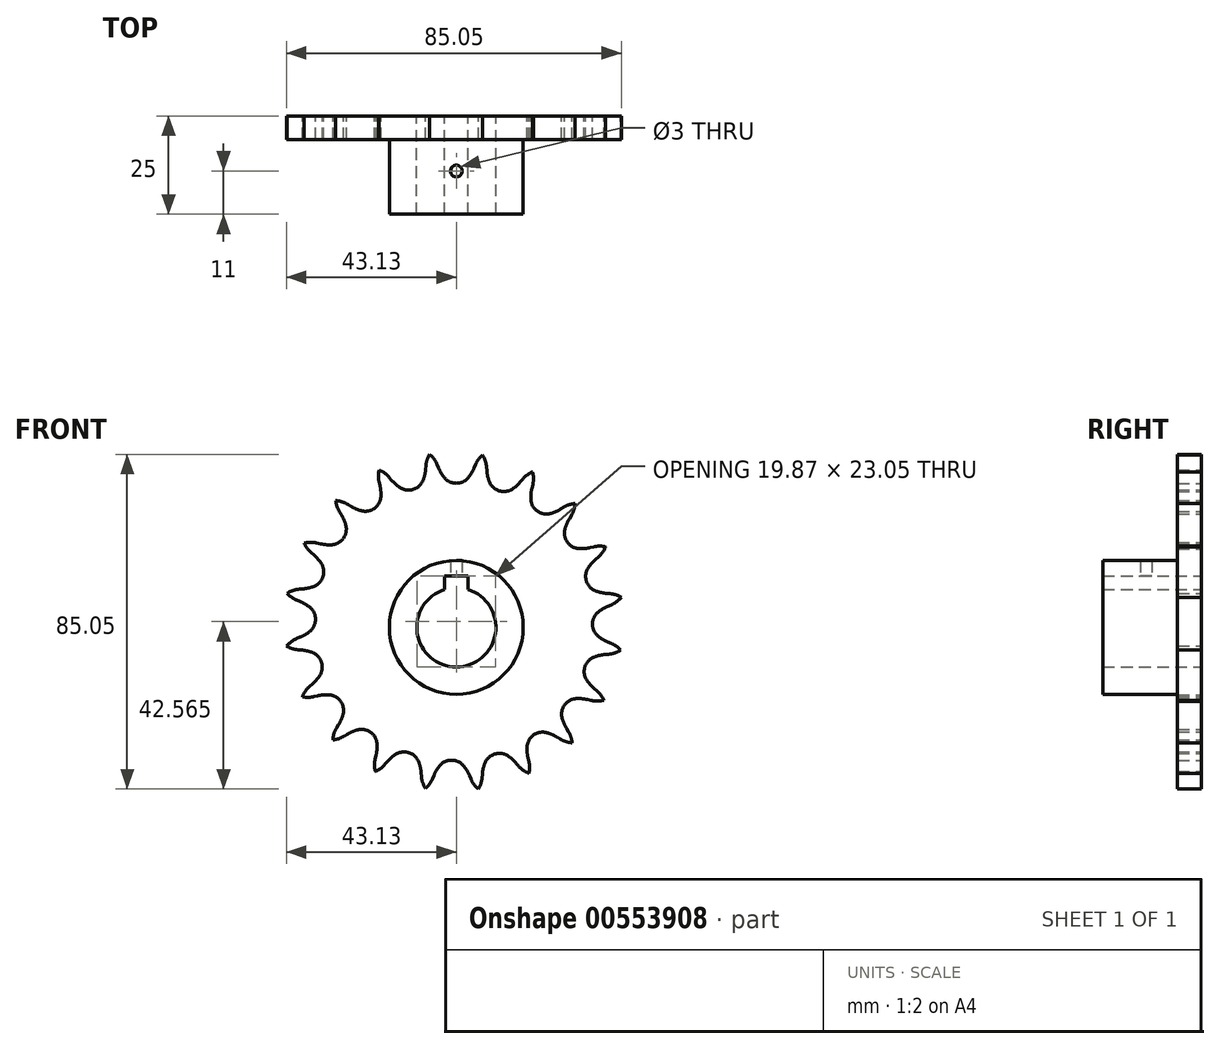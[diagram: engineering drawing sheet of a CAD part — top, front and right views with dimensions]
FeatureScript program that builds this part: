
annotation { "Feature Type Name" : "Feature", "Feature Type Description" : "" }
export const myFeature = defineFeature(function(context is Context, id is Id, definition is map)
    precondition{}
    {
        {
            var Q0;
            Q0=qCreatedBy(makeId("Front.planeOp"),FACE);
            var sketch = newSketch(context, id + "F0", { "sketchPlane" : qUnion([Q0])});
            skCircle(sketch, "E0", {"center": v(0, 0) * mm, "radius": 17 * mm});
            skCircle(sketch, "E1", {"center": v(0, 0) * mm, "radius": 10.05 * mm});
            skSolve(sketch);
        }
        {
            var Q0;
            Q0 = qSketchRegion(id + "F0", true);
            extrude(context, id + "F1", {"entities" : qUnion([Q0]), "depth" : 25 * mm, "offsetDistance" : 25 * mm});
        }
        {
            var Q0;
            Q0=qCreatedBy(makeId("Front.planeOp"),FACE);
            var sketch = newSketch(context, id + "F2", { "sketchPlane" : qUnion([Q0])});
            skCircle(sketch, "E2", {"center": v(0, 0) * mm, "radius": 40.6 * mm, "construction": true});
            skLineSegment(sketch, "E3", {"start": v(0, 0) * mm, "end": v(0, 40.6) * mm, "construction": true});
            skLineSegment(sketch, "E4", {"start": v(0, 40.6) * mm, "end": v(46.47, 40.6) * mm, "construction": true});
            skLineSegment(sketch, "E5", {"start": v(0, 40.6) * mm, "end": v(6.22, 44.3) * mm, "construction": true});
            skLineSegment(sketch, "E6", {"start": v(6.22, 44.3) * mm, "end": v(-5.45, 41.58) * mm, "construction": true});
            skLineSegment(sketch, "E7", {"start": v(-5.45, 41.58) * mm, "end": v(-7.28, 49.4) * mm, "construction": true});
            skSolve(sketch);
        }
        {
            var Q0;
            Q0=qCreatedBy(makeId("Front.planeOp"),FACE);
            var sketch = newSketch(context, id + "F3", { "sketchPlane" : qUnion([Q0])});
            skCircle(sketch, "E8", {"center": v(0, 0) * mm, "radius": 40.6 * mm, "construction": true});
            skLineSegment(sketch, "E9", {"start": v(0, 0) * mm, "end": v(0, 40.6) * mm, "construction": true});
            skLineSegment(sketch, "E10", {"start": v(0, 40.6) * mm, "end": v(62.23, 40.6) * mm, "construction": true});
            skArc(sketch, "E11", {"start": v(-3.14, 38.14) * mm, "mid": v(-1.75, 37.01) * mm, "end": v(0, 36.61) * mm});
            skLineSegment(sketch, "E12", {"start": v(0, 40.6) * mm, "end": v(5, 44.5) * mm, "construction": true});
            skLineSegment(sketch, "E13", {"start": v(5, 44.5) * mm, "end": v(-4.52, 40.5) * mm, "construction": true});
            skLineSegment(sketch, "E14", {"start": v(-4.52, 40.5) * mm, "end": v(-4.9, 41.4) * mm});
            skArc(sketch, "E15", {"start": v(-4.52, 40.5) * mm, "mid": v(-3.9, 39.27) * mm, "end": v(-3.14, 38.14) * mm});
            skArc(sketch, "E16", {"start": v(-4.9, 41.4) * mm, "mid": v(-5.76, 42.88) * mm, "end": v(-6.98, 44.09) * mm});
            skLineSegment(sketch, "E17", {"start": v(0, 0) * mm, "end": v(-9.35, 59.04) * mm, "construction": true});
            skLineSegment(sketch, "E18.trimOffspring", {"start": v(-7.56, 47.73) * mm, "end": v(-8.23, 49.33) * mm, "construction": true});
            skArc(sketch, "E19.trimOffspring", {"start": v(-3.98, 40.72) * mm, "mid": v(-3.98, 40.56) * mm, "end": v(-3.98, 40.4) * mm});
            skArc(sketch, "E20.trimOffspring", {"start": v(3.98, 40.4) * mm, "mid": v(3.98, 40.5) * mm, "end": v(3.98, 40.6) * mm});
            skArc(sketch, "E21.MirrorCS", {"start": v(3.14, 38.14) * mm, "mid": v(1.75, 37.01) * mm, "end": v(0, 36.61) * mm});
            skArc(sketch, "E22.MirrorCS", {"start": v(4.52, 40.5) * mm, "mid": v(3.9, 39.27) * mm, "end": v(3.14, 38.14) * mm});
            skLineSegment(sketch, "E23.MirrorCS", {"start": v(4.52, 40.5) * mm, "end": v(4.9, 41.4) * mm});
            skArc(sketch, "E24.MirrorCS", {"start": v(4.9, 41.4) * mm, "mid": v(5.76, 42.88) * mm, "end": v(6.98, 44.09) * mm});
            skArc(sketch, "E25.1.0", {"start": v(-17.04, 38.12) * mm, "mid": v(-18.32, 39.26) * mm, "end": v(-19.85, 40.03) * mm});
            skArc(sketch, "E25.1.1", {"start": v(-16.4, 37.37) * mm, "mid": v(-15.44, 36.4) * mm, "end": v(-14.36, 35.56) * mm});
            skArc(sketch, "E25.1.2", {"start": v(-14.36, 35.56) * mm, "mid": v(-12.68, 34.92) * mm, "end": v(-10.9, 35.08) * mm});
            skLineSegment(sketch, "E25.1.3", {"start": v(-16.4, 37.37) * mm, "end": v(-17.04, 38.12) * mm});
            skArc(sketch, "E25.1.4", {"start": v(-8.39, 37.5) * mm, "mid": v(-9.37, 36) * mm, "end": v(-10.9, 35.08) * mm});
            skArc(sketch, "E25.1.5", {"start": v(-7.8, 40.17) * mm, "mid": v(-8, 38.81) * mm, "end": v(-8.39, 37.5) * mm});
            skLineSegment(sketch, "E25.1.6", {"start": v(-7.8, 40.17) * mm, "end": v(-7.72, 41.14) * mm});
            skArc(sketch, "E25.1.7", {"start": v(-7.72, 41.14) * mm, "mid": v(-7.36, 42.82) * mm, "end": v(-6.57, 44.34) * mm});
            skArc(sketch, "E25.2.0", {"start": v(-27.57, 31.24) * mm, "mid": v(-29.14, 31.93) * mm, "end": v(-30.84, 32.19) * mm});
            skArc(sketch, "E25.2.1", {"start": v(-26.73, 30.73) * mm, "mid": v(-25.52, 30.1) * mm, "end": v(-24.23, 29.64) * mm});
            skArc(sketch, "E25.2.2", {"start": v(-24.23, 29.64) * mm, "mid": v(-22.44, 29.55) * mm, "end": v(-20.8, 30.25) * mm});
            skLineSegment(sketch, "E25.2.3", {"start": v(-26.73, 30.73) * mm, "end": v(-27.57, 31.24) * mm});
            skArc(sketch, "E25.2.4", {"start": v(-19.15, 33.33) * mm, "mid": v(-19.62, 31.6) * mm, "end": v(-20.8, 30.25) * mm});
            skArc(sketch, "E25.2.5", {"start": v(-19.42, 36.04) * mm, "mid": v(-19.2, 34.7) * mm, "end": v(-19.15, 33.33) * mm});
            skLineSegment(sketch, "E25.2.6", {"start": v(-19.42, 36.04) * mm, "end": v(-19.64, 37) * mm});
            skArc(sketch, "E25.2.7", {"start": v(-19.64, 37) * mm, "mid": v(-19.81, 38.7) * mm, "end": v(-19.54, 40.4) * mm});
            skArc(sketch, "E25.3.0", {"start": v(-35.46, 21.45) * mm, "mid": v(-37.17, 21.62) * mm, "end": v(-38.86, 21.34) * mm});
            skArc(sketch, "E25.3.1", {"start": v(-34.5, 21.22) * mm, "mid": v(-33.16, 21) * mm, "end": v(-31.8, 20.96) * mm});
            skArc(sketch, "E25.3.2", {"start": v(-31.8, 20.96) * mm, "mid": v(-30.06, 21.42) * mm, "end": v(-28.7, 22.6) * mm});
            skLineSegment(sketch, "E25.3.3", {"start": v(-34.5, 21.22) * mm, "end": v(-35.46, 21.45) * mm});
            skArc(sketch, "E25.3.4", {"start": v(-28.1, 26.03) * mm, "mid": v(-28, 24.25) * mm, "end": v(-28.7, 22.6) * mm});
            skArc(sketch, "E25.3.5", {"start": v(-29.2, 28.53) * mm, "mid": v(-28.57, 27.32) * mm, "end": v(-28.1, 26.03) * mm});
            skLineSegment(sketch, "E25.3.6", {"start": v(-29.2, 28.53) * mm, "end": v(-29.7, 29.38) * mm});
            skArc(sketch, "E25.3.7", {"start": v(-29.7, 29.38) * mm, "mid": v(-30.4, 30.95) * mm, "end": v(-30.65, 32.64) * mm});
            skArc(sketch, "E25.4.0", {"start": v(-39.94, 9.7) * mm, "mid": v(-41.62, 9.33) * mm, "end": v(-43.14, 8.54) * mm});
            skArc(sketch, "E25.4.1", {"start": v(-38.96, 9.78) * mm, "mid": v(-37.61, 9.98) * mm, "end": v(-36.3, 10.36) * mm});
            skArc(sketch, "E25.4.2", {"start": v(-36.3, 10.36) * mm, "mid": v(-34.8, 11.34) * mm, "end": v(-33.87, 12.88) * mm});
            skLineSegment(sketch, "E25.4.3", {"start": v(-38.96, 9.78) * mm, "end": v(-39.94, 9.7) * mm});
            skArc(sketch, "E25.4.4", {"start": v(-34.36, 16.33) * mm, "mid": v(-33.72, 14.66) * mm, "end": v(-33.87, 12.88) * mm});
            skArc(sketch, "E25.4.5", {"start": v(-36.17, 18.37) * mm, "mid": v(-35.2, 17.41) * mm, "end": v(-34.36, 16.33) * mm});
            skLineSegment(sketch, "E25.4.6", {"start": v(-36.17, 18.37) * mm, "end": v(-36.92, 19.01) * mm});
            skArc(sketch, "E25.4.7", {"start": v(-36.92, 19.01) * mm, "mid": v(-38.06, 20.3) * mm, "end": v(-38.83, 21.83) * mm});
            skArc(sketch, "E25.5.0", {"start": v(-40.57, -2.87) * mm, "mid": v(-42.05, -3.73) * mm, "end": v(-43.26, -4.95) * mm});
            skArc(sketch, "E25.5.1", {"start": v(-39.66, -2.48) * mm, "mid": v(-38.44, -1.87) * mm, "end": v(-37.31, -1.1) * mm});
            skArc(sketch, "E25.5.2", {"start": v(-37.31, -1.1) * mm, "mid": v(-36.18, 0.29) * mm, "end": v(-35.78, 2.03) * mm});
            skLineSegment(sketch, "E25.5.3", {"start": v(-39.66, -2.48) * mm, "end": v(-40.57, -2.87) * mm});
            skArc(sketch, "E25.5.4", {"start": v(-37.31, 5.17) * mm, "mid": v(-36.18, 3.78) * mm, "end": v(-35.78, 2.03) * mm});
            skArc(sketch, "E25.5.5", {"start": v(-39.66, 6.55) * mm, "mid": v(-38.44, 5.94) * mm, "end": v(-37.31, 5.17) * mm});
            skLineSegment(sketch, "E25.5.6", {"start": v(-39.66, 6.55) * mm, "end": v(-40.57, 6.93) * mm});
            skArc(sketch, "E25.5.7", {"start": v(-40.57, 6.93) * mm, "mid": v(-42.05, 7.8) * mm, "end": v(-43.26, 9.02) * mm});
            skArc(sketch, "E25.6.0", {"start": v(-37.29, -15) * mm, "mid": v(-38.43, -16.29) * mm, "end": v(-39.2, -17.82) * mm});
            skArc(sketch, "E25.6.1", {"start": v(-36.54, -14.36) * mm, "mid": v(-35.57, -13.4) * mm, "end": v(-34.73, -12.32) * mm});
            skArc(sketch, "E25.6.2", {"start": v(-34.73, -12.32) * mm, "mid": v(-34.09, -10.65) * mm, "end": v(-34.25, -8.87) * mm});
            skLineSegment(sketch, "E25.6.3", {"start": v(-36.54, -14.36) * mm, "end": v(-37.29, -15) * mm});
            skArc(sketch, "E25.6.4", {"start": v(-36.67, -6.36) * mm, "mid": v(-35.17, -7.33) * mm, "end": v(-34.25, -8.87) * mm});
            skArc(sketch, "E25.6.5", {"start": v(-39.34, -5.77) * mm, "mid": v(-37.98, -5.97) * mm, "end": v(-36.67, -6.36) * mm});
            skLineSegment(sketch, "E25.6.6", {"start": v(-39.34, -5.77) * mm, "end": v(-40.31, -5.69) * mm});
            skArc(sketch, "E25.6.7", {"start": v(-40.31, -5.69) * mm, "mid": v(-41.99, -5.32) * mm, "end": v(-43.51, -4.54) * mm});
            skArc(sketch, "E25.7.0", {"start": v(-30.41, -25.54) * mm, "mid": v(-31.1, -27.1) * mm, "end": v(-31.36, -28.8) * mm});
            skArc(sketch, "E25.7.1", {"start": v(-29.9, -24.7) * mm, "mid": v(-29.27, -23.48) * mm, "end": v(-28.8, -22.2) * mm});
            skArc(sketch, "E25.7.2", {"start": v(-28.8, -22.2) * mm, "mid": v(-28.72, -20.4) * mm, "end": v(-29.42, -18.76) * mm});
            skLineSegment(sketch, "E25.7.3", {"start": v(-29.9, -24.7) * mm, "end": v(-30.41, -25.54) * mm});
            skArc(sketch, "E25.7.4", {"start": v(-32.5, -17.12) * mm, "mid": v(-30.77, -17.58) * mm, "end": v(-29.42, -18.76) * mm});
            skArc(sketch, "E25.7.5", {"start": v(-35.21, -17.39) * mm, "mid": v(-33.86, -17.16) * mm, "end": v(-32.5, -17.12) * mm});
            skLineSegment(sketch, "E25.7.6", {"start": v(-35.21, -17.39) * mm, "end": v(-36.17, -17.61) * mm});
            skArc(sketch, "E25.7.7", {"start": v(-36.17, -17.61) * mm, "mid": v(-37.88, -17.78) * mm, "end": v(-39.57, -17.5) * mm});
            skArc(sketch, "E25.8.0", {"start": v(-20.62, -33.43) * mm, "mid": v(-20.79, -35.14) * mm, "end": v(-20.51, -36.83) * mm});
            skArc(sketch, "E25.8.1", {"start": v(-20.4, -32.47) * mm, "mid": v(-20.17, -31.12) * mm, "end": v(-20.13, -29.76) * mm});
            skArc(sketch, "E25.8.2", {"start": v(-20.13, -29.76) * mm, "mid": v(-20.6, -28.03) * mm, "end": v(-21.77, -26.67) * mm});
            skLineSegment(sketch, "E25.8.3", {"start": v(-20.4, -32.47) * mm, "end": v(-20.62, -33.43) * mm});
            skArc(sketch, "E25.8.4", {"start": v(-25.2, -26.07) * mm, "mid": v(-23.42, -25.98) * mm, "end": v(-21.77, -26.67) * mm});
            skArc(sketch, "E25.8.5", {"start": v(-27.7, -27.16) * mm, "mid": v(-26.5, -26.53) * mm, "end": v(-25.2, -26.07) * mm});
            skLineSegment(sketch, "E25.8.6", {"start": v(-27.7, -27.16) * mm, "end": v(-28.55, -27.67) * mm});
            skArc(sketch, "E25.8.7", {"start": v(-28.55, -27.67) * mm, "mid": v(-30.12, -28.36) * mm, "end": v(-31.8, -28.62) * mm});
            skArc(sketch, "E25.9.0", {"start": v(-8.87, -37.9) * mm, "mid": v(-8.5, -39.58) * mm, "end": v(-7.71, -41.1) * mm});
            skArc(sketch, "E25.9.1", {"start": v(-8.95, -36.93) * mm, "mid": v(-9.15, -35.58) * mm, "end": v(-9.53, -34.26) * mm});
            skArc(sketch, "E25.9.2", {"start": v(-9.53, -34.26) * mm, "mid": v(-10.5, -32.76) * mm, "end": v(-12.05, -31.84) * mm});
            skLineSegment(sketch, "E25.9.3", {"start": v(-8.95, -36.93) * mm, "end": v(-8.87, -37.9) * mm});
            skArc(sketch, "E25.9.4", {"start": v(-15.5, -32.33) * mm, "mid": v(-13.83, -31.68) * mm, "end": v(-12.05, -31.84) * mm});
            skArc(sketch, "E25.9.5", {"start": v(-17.54, -34.14) * mm, "mid": v(-16.58, -33.16) * mm, "end": v(-15.5, -32.33) * mm});
            skLineSegment(sketch, "E25.9.6", {"start": v(-17.54, -34.14) * mm, "end": v(-18.18, -34.88) * mm});
            skArc(sketch, "E25.9.7", {"start": v(-18.18, -34.88) * mm, "mid": v(-19.46, -36.02) * mm, "end": v(-21, -36.8) * mm});
            skArc(sketch, "E25.10.0", {"start": v(3.7, -38.54) * mm, "mid": v(4.56, -40.02) * mm, "end": v(5.78, -41.22) * mm});
            skArc(sketch, "E25.10.1", {"start": v(3.31, -37.63) * mm, "mid": v(2.7, -36.4) * mm, "end": v(1.93, -35.28) * mm});
            skArc(sketch, "E25.10.2", {"start": v(1.93, -35.28) * mm, "mid": v(0.54, -34.15) * mm, "end": v(-1.2, -33.75) * mm});
            skLineSegment(sketch, "E25.10.3", {"start": v(3.31, -37.63) * mm, "end": v(3.7, -38.54) * mm});
            skArc(sketch, "E25.10.4", {"start": v(-4.34, -35.28) * mm, "mid": v(-2.95, -34.15) * mm, "end": v(-1.2, -33.75) * mm});
            skArc(sketch, "E25.10.5", {"start": v(-5.72, -37.63) * mm, "mid": v(-5.1, -36.4) * mm, "end": v(-4.34, -35.28) * mm});
            skLineSegment(sketch, "E25.10.6", {"start": v(-5.72, -37.63) * mm, "end": v(-6.1, -38.54) * mm});
            skArc(sketch, "E25.10.7", {"start": v(-6.1, -38.54) * mm, "mid": v(-6.97, -40.02) * mm, "end": v(-8.19, -41.22) * mm});
            skArc(sketch, "E25.11.0", {"start": v(15.84, -35.25) * mm, "mid": v(17.12, -36.4) * mm, "end": v(18.65, -37.16) * mm});
            skArc(sketch, "E25.11.1", {"start": v(15.2, -34.5) * mm, "mid": v(14.23, -33.54) * mm, "end": v(13.15, -32.7) * mm});
            skArc(sketch, "E25.11.2", {"start": v(13.15, -32.7) * mm, "mid": v(11.48, -32.06) * mm, "end": v(9.7, -32.21) * mm});
            skLineSegment(sketch, "E25.11.3", {"start": v(15.2, -34.5) * mm, "end": v(15.84, -35.25) * mm});
            skArc(sketch, "E25.11.4", {"start": v(7.19, -34.64) * mm, "mid": v(8.16, -33.13) * mm, "end": v(9.7, -32.21) * mm});
            skArc(sketch, "E25.11.5", {"start": v(6.6, -37.3) * mm, "mid": v(6.8, -35.95) * mm, "end": v(7.19, -34.64) * mm});
            skLineSegment(sketch, "E25.11.6", {"start": v(6.6, -37.3) * mm, "end": v(6.52, -38.28) * mm});
            skArc(sketch, "E25.11.7", {"start": v(6.52, -38.28) * mm, "mid": v(6.15, -39.96) * mm, "end": v(5.37, -41.48) * mm});
            skArc(sketch, "E25.12.0", {"start": v(26.37, -28.38) * mm, "mid": v(27.94, -29.07) * mm, "end": v(29.63, -29.33) * mm});
            skArc(sketch, "E25.12.1", {"start": v(25.53, -27.87) * mm, "mid": v(24.31, -27.24) * mm, "end": v(23.03, -26.78) * mm});
            skArc(sketch, "E25.12.2", {"start": v(23.03, -26.78) * mm, "mid": v(21.24, -26.68) * mm, "end": v(19.59, -27.38) * mm});
            skLineSegment(sketch, "E25.12.3", {"start": v(25.53, -27.87) * mm, "end": v(26.37, -28.38) * mm});
            skArc(sketch, "E25.12.4", {"start": v(17.95, -30.46) * mm, "mid": v(18.41, -28.73) * mm, "end": v(19.59, -27.38) * mm});
            skArc(sketch, "E25.12.5", {"start": v(18.22, -33.18) * mm, "mid": v(18, -31.83) * mm, "end": v(17.95, -30.46) * mm});
            skLineSegment(sketch, "E25.12.6", {"start": v(18.22, -33.18) * mm, "end": v(18.44, -34.14) * mm});
            skArc(sketch, "E25.12.7", {"start": v(18.44, -34.14) * mm, "mid": v(18.61, -35.84) * mm, "end": v(18.33, -37.53) * mm});
            skArc(sketch, "E25.13.0", {"start": v(34.26, -18.58) * mm, "mid": v(35.97, -18.76) * mm, "end": v(37.66, -18.48) * mm});
            skArc(sketch, "E25.13.1", {"start": v(33.3, -18.36) * mm, "mid": v(31.95, -18.14) * mm, "end": v(30.59, -18.1) * mm});
            skArc(sketch, "E25.13.2", {"start": v(30.59, -18.1) * mm, "mid": v(28.86, -18.56) * mm, "end": v(27.5, -19.73) * mm});
            skLineSegment(sketch, "E25.13.3", {"start": v(33.3, -18.36) * mm, "end": v(34.26, -18.58) * mm});
            skArc(sketch, "E25.13.4", {"start": v(26.9, -23.17) * mm, "mid": v(26.8, -21.38) * mm, "end": v(27.5, -19.73) * mm});
            skArc(sketch, "E25.13.5", {"start": v(28, -25.67) * mm, "mid": v(27.36, -24.46) * mm, "end": v(26.9, -23.17) * mm});
            skLineSegment(sketch, "E25.13.6", {"start": v(28, -25.67) * mm, "end": v(28.5, -26.51) * mm});
            skArc(sketch, "E25.13.7", {"start": v(28.5, -26.51) * mm, "mid": v(29.19, -28.08) * mm, "end": v(29.45, -29.78) * mm});
            skArc(sketch, "E25.14.0", {"start": v(38.74, -6.83) * mm, "mid": v(40.41, -6.47) * mm, "end": v(41.94, -5.68) * mm});
            skArc(sketch, "E25.14.1", {"start": v(37.76, -6.91) * mm, "mid": v(36.4, -7.12) * mm, "end": v(35.1, -7.5) * mm});
            skArc(sketch, "E25.14.2", {"start": v(35.1, -7.5) * mm, "mid": v(33.6, -8.48) * mm, "end": v(32.67, -10.01) * mm});
            skLineSegment(sketch, "E25.14.3", {"start": v(37.76, -6.91) * mm, "end": v(38.74, -6.83) * mm});
            skArc(sketch, "E25.14.4", {"start": v(33.16, -13.47) * mm, "mid": v(32.51, -11.8) * mm, "end": v(32.67, -10.01) * mm});
            skArc(sketch, "E25.14.5", {"start": v(34.97, -15.5) * mm, "mid": v(34, -14.55) * mm, "end": v(33.16, -13.47) * mm});
            skLineSegment(sketch, "E25.14.6", {"start": v(34.97, -15.5) * mm, "end": v(35.71, -16.15) * mm});
            skArc(sketch, "E25.14.7", {"start": v(35.71, -16.15) * mm, "mid": v(36.85, -17.43) * mm, "end": v(37.62, -18.96) * mm});
            skArc(sketch, "E25.15.0", {"start": v(39.37, 5.73) * mm, "mid": v(40.85, 6.6) * mm, "end": v(42.05, 7.81) * mm});
            skArc(sketch, "E25.15.1", {"start": v(38.46, 5.35) * mm, "mid": v(37.24, 4.74) * mm, "end": v(36.1, 3.97) * mm});
            skArc(sketch, "E25.15.2", {"start": v(36.1, 3.97) * mm, "mid": v(34.98, 2.58) * mm, "end": v(34.58, 0.83) * mm});
            skLineSegment(sketch, "E25.15.3", {"start": v(38.46, 5.35) * mm, "end": v(39.37, 5.73) * mm});
            skArc(sketch, "E25.15.4", {"start": v(36.1, -2.3) * mm, "mid": v(34.98, -0.92) * mm, "end": v(34.58, 0.83) * mm});
            skArc(sketch, "E25.15.5", {"start": v(38.46, -3.69) * mm, "mid": v(37.24, -3.08) * mm, "end": v(36.1, -2.3) * mm});
            skLineSegment(sketch, "E25.15.6", {"start": v(38.46, -3.69) * mm, "end": v(39.37, -4.07) * mm});
            skArc(sketch, "E25.15.7", {"start": v(39.37, -4.07) * mm, "mid": v(40.85, -4.93) * mm, "end": v(42.05, -6.15) * mm});
            skArc(sketch, "E25.16.0", {"start": v(36.08, 17.87) * mm, "mid": v(37.22, 19.15) * mm, "end": v(38, 20.68) * mm});
            skArc(sketch, "E25.16.1", {"start": v(35.34, 17.23) * mm, "mid": v(34.37, 16.27) * mm, "end": v(33.53, 15.19) * mm});
            skArc(sketch, "E25.16.2", {"start": v(33.53, 15.19) * mm, "mid": v(32.89, 13.51) * mm, "end": v(33.04, 11.73) * mm});
            skLineSegment(sketch, "E25.16.3", {"start": v(35.34, 17.23) * mm, "end": v(36.08, 17.87) * mm});
            skArc(sketch, "E25.16.4", {"start": v(35.47, 9.22) * mm, "mid": v(33.96, 10.2) * mm, "end": v(33.04, 11.73) * mm});
            skArc(sketch, "E25.16.5", {"start": v(38.13, 8.63) * mm, "mid": v(36.78, 8.84) * mm, "end": v(35.47, 9.22) * mm});
            skLineSegment(sketch, "E25.16.6", {"start": v(38.13, 8.63) * mm, "end": v(39.11, 8.55) * mm});
            skArc(sketch, "E25.16.7", {"start": v(39.11, 8.55) * mm, "mid": v(40.79, 8.19) * mm, "end": v(42.3, 7.4) * mm});
            skArc(sketch, "E25.17.0", {"start": v(29.2, 28.4) * mm, "mid": v(29.9, 29.97) * mm, "end": v(30.16, 31.67) * mm});
            skArc(sketch, "E25.17.1", {"start": v(28.7, 27.56) * mm, "mid": v(28.07, 26.35) * mm, "end": v(27.6, 25.06) * mm});
            skArc(sketch, "E25.17.2", {"start": v(27.6, 25.06) * mm, "mid": v(27.51, 23.27) * mm, "end": v(28.21, 21.62) * mm});
            skLineSegment(sketch, "E25.17.3", {"start": v(28.7, 27.56) * mm, "end": v(29.2, 28.4) * mm});
            skArc(sketch, "E25.17.4", {"start": v(31.3, 19.98) * mm, "mid": v(29.56, 20.45) * mm, "end": v(28.21, 21.62) * mm});
            skArc(sketch, "E25.17.5", {"start": v(34.01, 20.25) * mm, "mid": v(32.66, 20.03) * mm, "end": v(31.3, 19.98) * mm});
            skLineSegment(sketch, "E25.17.6", {"start": v(34.01, 20.25) * mm, "end": v(34.97, 20.47) * mm});
            skArc(sketch, "E25.17.7", {"start": v(34.97, 20.47) * mm, "mid": v(36.67, 20.64) * mm, "end": v(38.36, 20.37) * mm});
            skArc(sketch, "E25.18.0", {"start": v(19.41, 36.3) * mm, "mid": v(19.59, 38) * mm, "end": v(19.3, 39.7) * mm});
            skArc(sketch, "E25.18.1", {"start": v(19.2, 35.34) * mm, "mid": v(18.97, 33.99) * mm, "end": v(18.92, 32.62) * mm});
            skArc(sketch, "E25.18.2", {"start": v(18.92, 32.62) * mm, "mid": v(19.39, 30.9) * mm, "end": v(20.56, 29.54) * mm});
            skLineSegment(sketch, "E25.18.3", {"start": v(19.2, 35.34) * mm, "end": v(19.41, 36.3) * mm});
            skArc(sketch, "E25.18.4", {"start": v(24, 28.93) * mm, "mid": v(22.21, 28.84) * mm, "end": v(20.56, 29.54) * mm});
            skArc(sketch, "E25.18.5", {"start": v(26.5, 30.02) * mm, "mid": v(25.29, 29.4) * mm, "end": v(24, 28.93) * mm});
            skLineSegment(sketch, "E25.18.6", {"start": v(26.5, 30.02) * mm, "end": v(27.34, 30.53) * mm});
            skArc(sketch, "E25.18.7", {"start": v(27.34, 30.53) * mm, "mid": v(28.91, 31.22) * mm, "end": v(30.6, 31.48) * mm});
            skArc(sketch, "E25.19.0", {"start": v(7.66, 40.77) * mm, "mid": v(7.3, 42.45) * mm, "end": v(6.51, 43.97) * mm});
            skArc(sketch, "E25.19.1", {"start": v(7.74, 39.8) * mm, "mid": v(7.95, 38.44) * mm, "end": v(8.33, 37.13) * mm});
            skArc(sketch, "E25.19.2", {"start": v(8.33, 37.13) * mm, "mid": v(9.3, 35.63) * mm, "end": v(10.84, 34.7) * mm});
            skLineSegment(sketch, "E25.19.3", {"start": v(7.74, 39.8) * mm, "end": v(7.66, 40.77) * mm});
            skArc(sketch, "E25.19.4", {"start": v(14.3, 35.19) * mm, "mid": v(12.63, 34.55) * mm, "end": v(10.84, 34.7) * mm});
            skArc(sketch, "E25.19.5", {"start": v(16.34, 37) * mm, "mid": v(15.38, 36.03) * mm, "end": v(14.3, 35.19) * mm});
            skLineSegment(sketch, "E25.19.6", {"start": v(16.34, 37) * mm, "end": v(16.98, 37.74) * mm});
            skArc(sketch, "E25.19.7", {"start": v(16.98, 37.74) * mm, "mid": v(18.26, 38.89) * mm, "end": v(19.8, 39.66) * mm});
            skPoint(sketch, "E25.center", {"position": v(-0.6, 1.43) * mm});
            skCircle(sketch, "E26", {"center": v(0, 0) * mm, "radius": 10.05 * mm});
            skSolve(sketch);
        }
        {
            var Q0;
            Q0=makeQuery(id+"F3.imprint","IMPRINT",FACE,{"disambiguationData":[TD([[makeQuery(id+"F3.imprint","IMPRINT",EDGE,{"derivedFrom":sQuery(id+"F3.wireOp",EDGE,"E11")}),-1.0]])]});
            extrude(context, id + "F4", {"entities" : qUnion([Q0]), "operationType" : NewBodyOperationType.ADD, "depth" : 6 * mm, "offsetDistance" : 25 * mm});
        }
        {
            var Q0;
            Q0=qCreatedBy(makeId("Front.planeOp"),FACE);
            var sketch = newSketch(context, id + "F5", { "sketchPlane" : qUnion([Q0])});
            skLineSegment(sketch, "E27.bottom", {"start": v(-3, 13) * mm, "end": v(3, 13) * mm});
            skLineSegment(sketch, "E27.top", {"start": v(-3, 0) * mm, "end": v(3, 0) * mm});
            skLineSegment(sketch, "E27.left", {"start": v(-3, 13) * mm, "end": v(-3, 0) * mm});
            skLineSegment(sketch, "E27.right", {"start": v(3, 13) * mm, "end": v(3, 0) * mm});
            skSolve(sketch);
        }
        {
            var Q0;
            Q0 = qSketchRegion(id + "F5", true);
            extrude(context, id + "F6", {"entities" : qUnion([Q0]), "operationType" : NewBodyOperationType.REMOVE, "depth" : 25 * mm, "offsetDistance" : 25 * mm});
        }
        {
            var Q0;
            Q0=qCreatedBy(makeId("Top.planeOp"),FACE);
            var sketch = newSketch(context, id + "F7", { "sketchPlane" : qUnion([Q0])});
            skCircle(sketch, "E28", {"center": v(0, -14) * mm, "radius": 1.5 * mm});
            skSolve(sketch);
        }
        {
            var Q0;
            Q0 = qSketchRegion(id + "F7", true);
            extrude(context, id + "F8", {"entities" : qUnion([Q0]), "operationType" : NewBodyOperationType.REMOVE, "endBound" : BoundingType.THROUGH_ALL, "depth" : 25 * mm, "offsetDistance" : 25 * mm});
        }
    });
